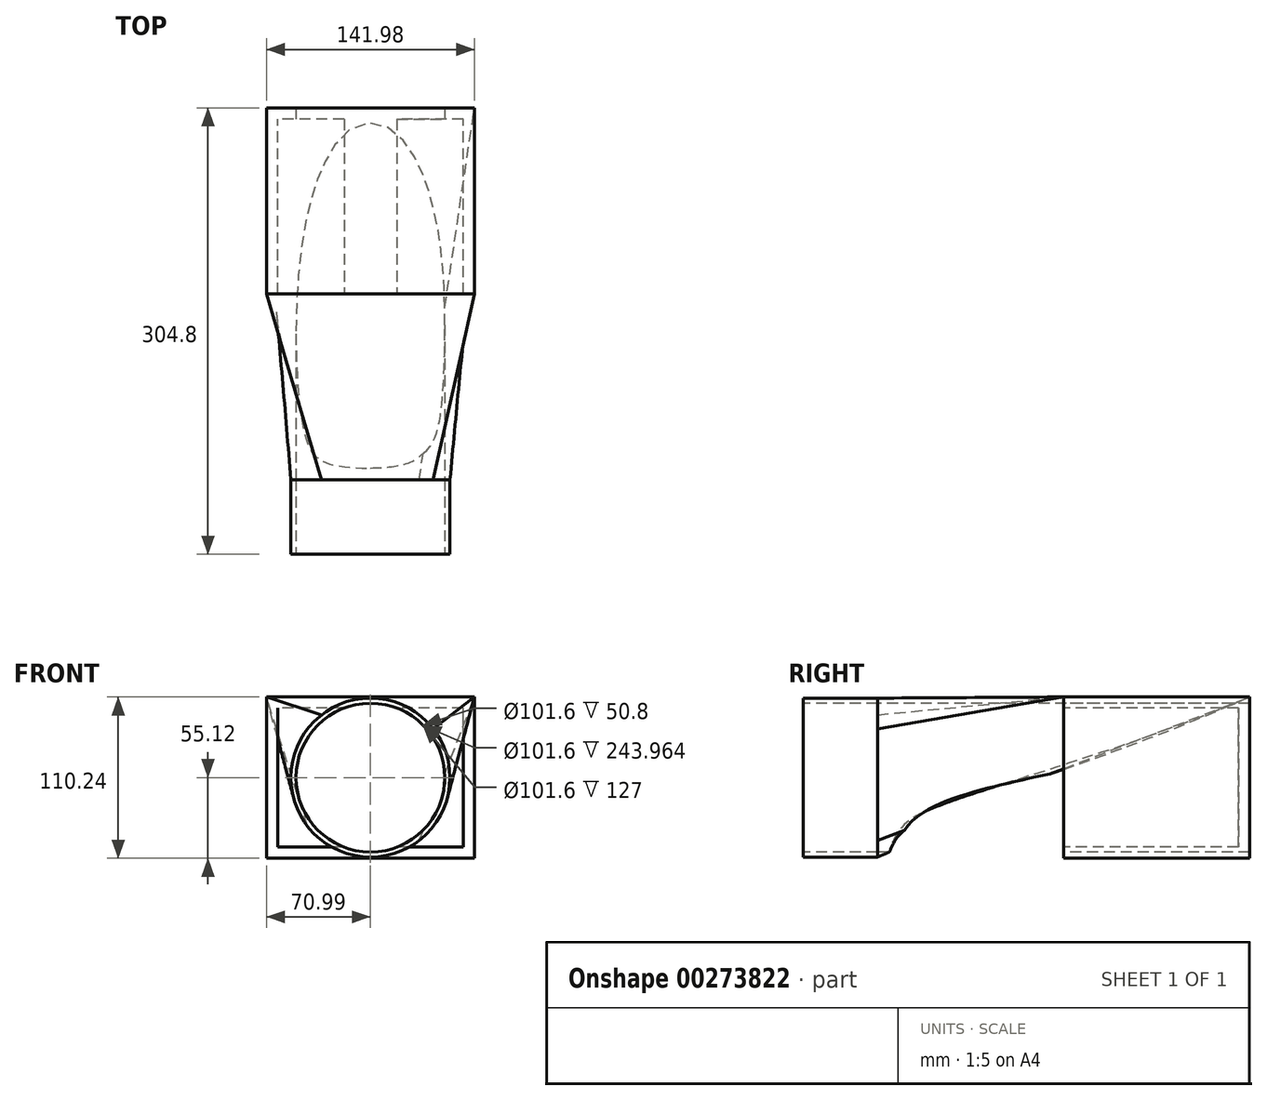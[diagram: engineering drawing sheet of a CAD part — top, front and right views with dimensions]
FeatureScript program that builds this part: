
annotation { "Feature Type Name" : "Feature", "Feature Type Description" : "" }
export const myFeature = defineFeature(function(context is Context, id is Id, definition is map)
    precondition{}
    {
        {
            var Q0;
            Q0=qCreatedBy(makeId("Front.planeOp"),FACE);
            var sketch = newSketch(context, id + "F0", { "sketchPlane" : qUnion([Q0])});
            skLineSegment(sketch, "E0", {"start": v(0, 86.67) * mm, "end": v(0, -87.31) * mm, "construction": true});
            skLineSegment(sketch, "E1.bottom", {"start": v(71, -55.12) * mm, "end": v(-71, -55.12) * mm});
            skLineSegment(sketch, "E1.top", {"start": v(71, 55.12) * mm, "end": v(-71, 55.12) * mm});
            skLineSegment(sketch, "E1.left", {"start": v(71, -55.12) * mm, "end": v(71, 55.12) * mm});
            skLineSegment(sketch, "E1.right", {"start": v(-71, -55.12) * mm, "end": v(-71, 55.12) * mm});
            skPoint(sketch, "E1.middle", {"position": v(0, 0) * mm});
            skSolve(sketch);
        }
        {
            var Q0;
            Q0=makeQuery(id+"F0.imprint","IMPRINT",FACE,{"disambiguationData":[TD([[makeQuery(id+"F0.imprint","IMPRINT",EDGE,{"derivedFrom":sQuery(id+"F0.wireOp",EDGE,"E1.bottom")}),-1.0]])]});
            extrude(context, id + "F1", {"entities" : qUnion([Q0]), "depth" : 127 * mm});
        }
        {
            var Q0;
            Q0=makeQuery(id+"F1.opExtrude","CAP_FACE",FACE,{"disambiguationData":[OSD([sQuery(id+"F0.wireOp",EDGE,"E1.bottom"),sQuery(id+"F0.wireOp",EDGE,"E1.top"),sQuery(id+"F0.wireOp",EDGE,"E1.left"),sQuery(id+"F0.wireOp",EDGE,"E1.right")])],"isStart":false});
            shell(context, id + "F2", {"entities" : qUnion([Q0]), "thickness" : 7.62 * mm});
        }
        {
            var Q0;
            Q0=makeQuery(id+"F1.opExtrude","CAP_FACE",FACE,{"disambiguationData":[OSD([sQuery(id+"F0.wireOp",EDGE,"E1.bottom"),sQuery(id+"F0.wireOp",EDGE,"E1.top"),sQuery(id+"F0.wireOp",EDGE,"E1.left"),sQuery(id+"F0.wireOp",EDGE,"E1.right")])],"isStart":false});
            cPlane(context, id + "F3", {"entities" : qUnion([Q0]), "cplaneType" : CPlaneType.OFFSET, "offset" : 127 * mm, "width" : 152.4 * mm, "height" : 152.4 * mm});
        }
        {
            var Q0;
            Q0=qCreatedBy(id+"F3.planeOp",FACE);
            var sketch = newSketch(context, id + "F4", { "sketchPlane" : qUnion([Q0])});
            skCircle(sketch, "E2", {"center": v(0, 0) * mm, "radius": 54.3 * mm});
            skSolve(sketch);
        }
        {
            var Q0;
            Q0=makeQuery(id+"F4.imprint","IMPRINT",FACE,{"disambiguationData":[TD([[makeQuery(id+"F4.imprint","IMPRINT",EDGE,{"derivedFrom":sQuery(id+"F4.wireOp",EDGE,"E2")}),1.0]])]});
            extrude(context, id + "F5", {"entities" : qUnion([Q0]), "depth" : 50.8 * mm});
        }
        {
            var Q0;
            Q0=makeQuery(id+"F5.opExtrude","CAP_FACE",FACE,{"disambiguationData":[OSD([sQuery(id+"F4.wireOp",EDGE,"E2")])],"isStart":true});
            var Q1;
            Q1=makeQuery(id+"F1.opExtrude","SWEPT_FACE",FACE,{"disambiguationData":[OSD([sQuery(id+"F0.wireOp",EDGE,"E1.top")])]});
            loft(context, id + "F6", {"sheetProfilesArray" : [{ "sheetProfileEntities" : qUnion([Q0]) }, { "sheetProfileEntities" : qUnion([Q1]) }]});
        }
        {
            var Q0;
            Q0=makeQuery(id+"F5.opExtrude","CAP_FACE",FACE,{"disambiguationData":[OSD([sQuery(id+"F4.wireOp",EDGE,"E2")])],"isStart":false});
            var sketch = newSketch(context, id + "F7", { "sketchPlane" : qUnion([Q0])});
            skPoint(sketch, "E3", {"position": v(0, 0) * mm});
            skSolve(sketch);
        }
        {
            var Q0;
            Q0=sQuery(id+"F7.wireOp",VERTEX,"E3");
            var Q1;
            Q1=makeQuery(id+"F1.opExtrude","SWEPT_BODY",BODY,{"disambiguationData":[OSD([sQuery(id+"F0.wireOp",EDGE,"E1.bottom"),sQuery(id+"F0.wireOp",EDGE,"E1.top"),sQuery(id+"F0.wireOp",EDGE,"E1.left"),sQuery(id+"F0.wireOp",EDGE,"E1.right")])]});
            var Q2;
            Q2=makeQuery(id+"F5.opExtrude","SWEPT_BODY",BODY,{"disambiguationData":[OSD([sQuery(id+"F4.wireOp",EDGE,"E2")])]});
            var Q3;
            Q3=makeQuery(id+"F6.opLoft","SWEPT_BODY",BODY,{"disambiguationData":[OSD([sQuery(id+"F0.wireOp",EDGE,"E1.top"),sQuery(id+"F4.wireOp",EDGE,"E2")])]});
            hole(context, id + "F8", {"style" : HoleStyle.SIMPLE, "endStyle" : HoleEndStyle.THROUGH, "holeDiameter" : 101.6 * mm, "tappedDepth" : 12.7 * mm, "tapClearance" : 3, "locations" : qUnion([Q0]), "scope" : qUnion([Q1, Q2, Q3])});
        }
    });
